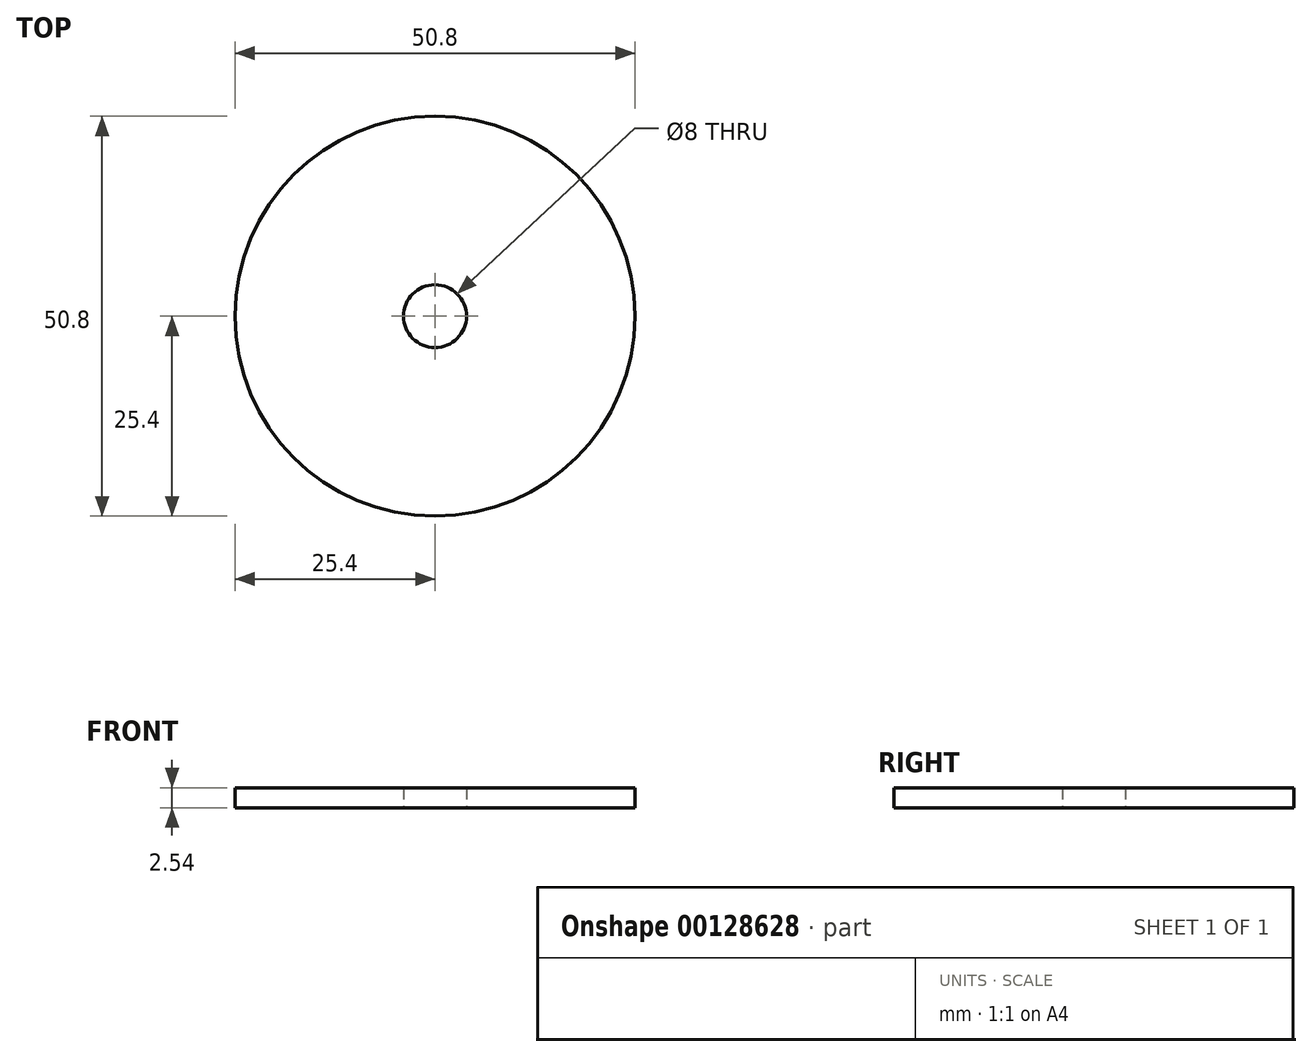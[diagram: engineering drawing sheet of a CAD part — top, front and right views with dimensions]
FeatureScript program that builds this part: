
annotation { "Feature Type Name" : "Feature", "Feature Type Description" : "" }
export const myFeature = defineFeature(function(context is Context, id is Id, definition is map)
    precondition{}
    {
        {
            var Q0;
            Q0=qCreatedBy(makeId("Top.planeOp"),FACE);
            var sketch = newSketch(context, id + "F0", { "sketchPlane" : qUnion([Q0])});
            skCircle(sketch, "E0", {"center": v(0, 0) * mm, "radius": 25.4 * mm});
            skCircle(sketch, "E1", {"center": v(0, 0) * mm, "radius": 4 * mm});
            skSolve(sketch);
        }
        {
            var Q0;
            Q0=makeQuery(id+"F0.imprint","IMPRINT",FACE,{"disambiguationData":[TD([[makeQuery(id+"F0.imprint","IMPRINT",EDGE,{"derivedFrom":sQuery(id+"F0.wireOp",EDGE,"E0")}),1.0]])]});
            extrude(context, id + "F1", {"entities" : qUnion([Q0]), "depth" : 2.54 * mm});
        }
    });
